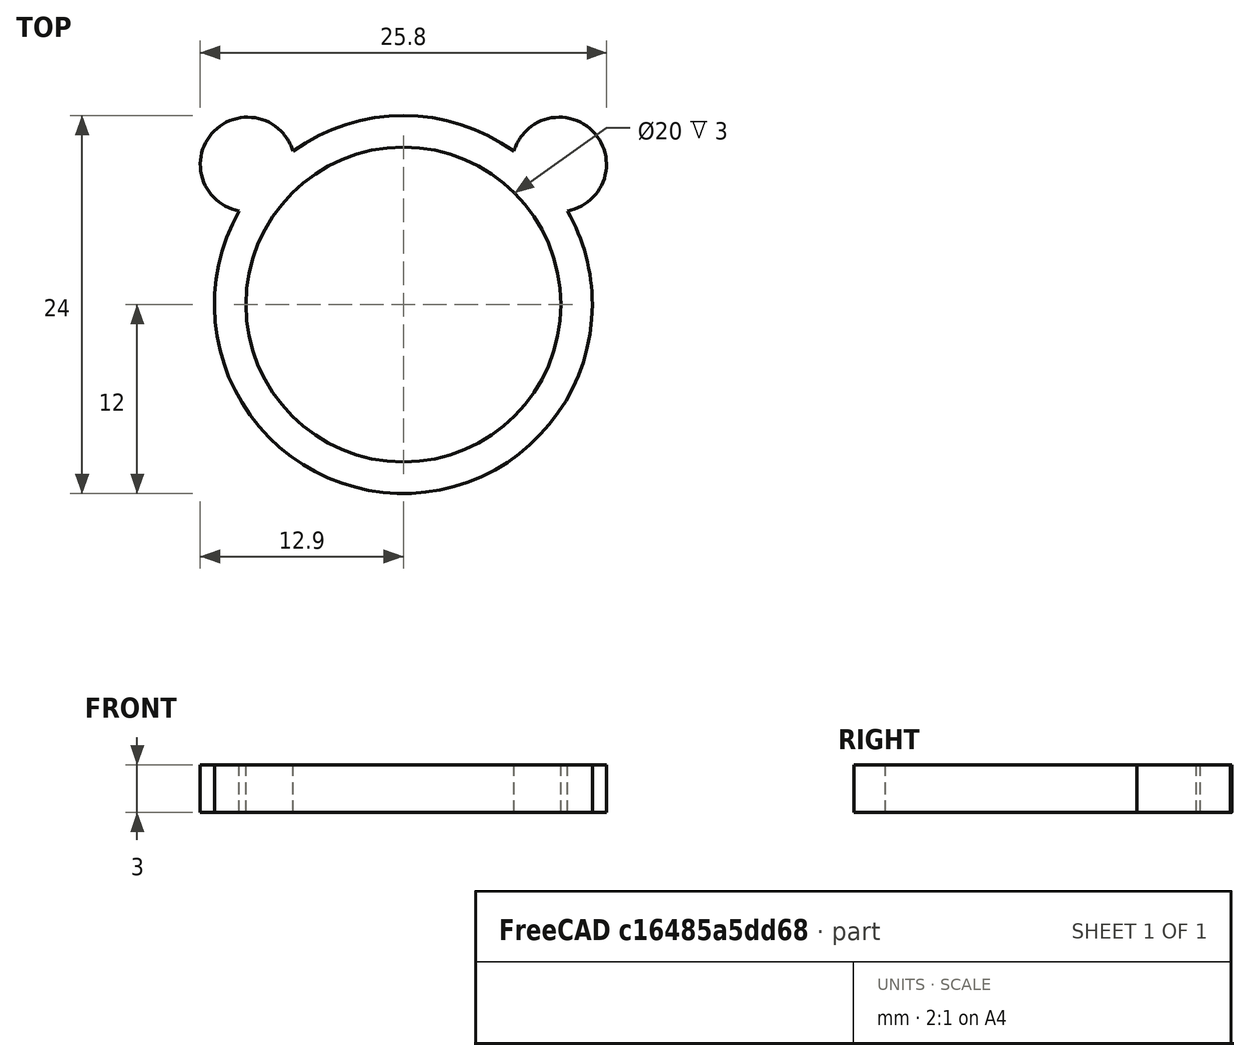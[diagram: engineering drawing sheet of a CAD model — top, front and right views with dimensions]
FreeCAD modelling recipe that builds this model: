
FCSTD DOCUMENT  (FreeCAD 0.17R12412 (Git))
Label: 01-ring-ears
License: All rights reserved
LicenseURL: http://en.wikipedia.org/wiki/All_rights_reserved
objects: Part::Cylinder×3, Part::Mirroring×1, Part::MultiFuse×1, Part::Cut×1
note: 6 computed .brp shape members not serialized (recipe doc carries the construction recipe); baked Part::Feature solids carry a one-line shape summary decoded from their .brp

FEATURE [Part::Cylinder] Cylinder  label="base-cylinder"
  Angle = 360
  AttacherType = Attacher::AttachEngine3D
  Height = 3
  Radius = 12
FEATURE [Part::Cylinder] Cylinder001  label="left-ear"
  Angle = 360
  AttacherType = Attacher::AttachEngine3D
  Height = 3
  Placement = pos=(-9.89949,8.89949,0) rot=(0,0,1;0.785398rad)
  Radius = 3
FEATURE [Part::Mirroring] Part__Mirroring  label="right-ear"
  Base = (0,0,0)
  Normal = (1,0,0)
  Source = -> Cylinder001
FEATURE [Part::MultiFuse] Fusion  label="ring-body"
  Shapes = -> [Cylinder001,Part__Mirroring,Cylinder]
FEATURE [Part::Cylinder] Cylinder002  label="hole"
  Angle = 360
  AttacherType = Attacher::AttachEngine3D
  Height = 10
  Placement = pos=(0,0,-4) rot=(0,0,1;0rad)
  Radius = 10
FEATURE [Part::Cut] Cut  label="ring-with-ears"
  Base = -> Fusion
  Tool = -> Cylinder002
